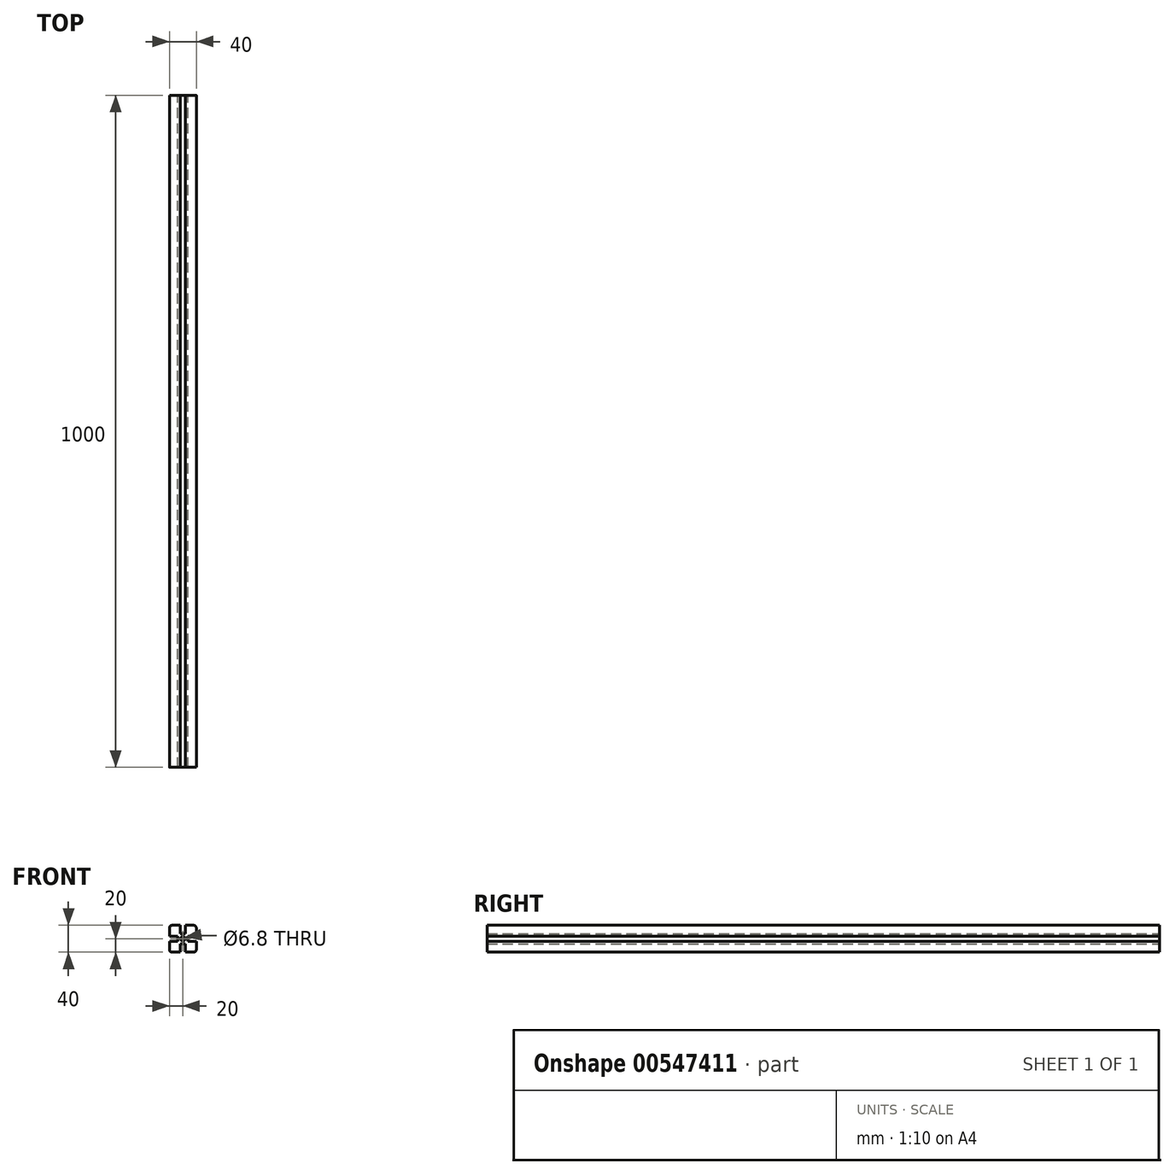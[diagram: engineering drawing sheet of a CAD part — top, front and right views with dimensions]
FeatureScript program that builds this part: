
annotation { "Feature Type Name" : "Feature", "Feature Type Description" : "" }
export const myFeature = defineFeature(function(context is Context, id is Id, definition is map)
    precondition{}
    {
        {
            var Q0;
            Q0=qCreatedBy(makeId("Front.planeOp"),FACE);
            var sketch = newSketch(context, id + "F0", { "sketchPlane" : qUnion([Q0])});
            skLineSegment(sketch, "E0.bottom", {"start": v(20, 20) * mm, "end": v(4, 20) * mm});
            skLineSegment(sketch, "E0.top", {"start": v(20, -20) * mm, "end": v(4, -20) * mm});
            skLineSegment(sketch, "E0.left", {"start": v(20, 20) * mm, "end": v(20, 4) * mm});
            skLineSegment(sketch, "E0.right", {"start": v(-20, 20) * mm, "end": v(-20, 4) * mm});
            skPoint(sketch, "E0.middle", {"position": v(0, 0) * mm});
            skLineSegment(sketch, "E1", {"start": v(20, 4) * mm, "end": v(7.75, 4) * mm});
            skLineSegment(sketch, "E2", {"start": v(7.75, 4) * mm, "end": v(7.75, -4) * mm});
            skLineSegment(sketch, "E3", {"start": v(7.75, -4) * mm, "end": v(20, -4) * mm});
            skLineSegment(sketch, "E4.top", {"start": v(-4, 7.75) * mm, "end": v(4, 7.75) * mm});
            skLineSegment(sketch, "E4.left", {"start": v(-4, 20) * mm, "end": v(-4, 7.75) * mm});
            skLineSegment(sketch, "E4.right", {"start": v(4, 20) * mm, "end": v(4, 7.75) * mm});
            skLineSegment(sketch, "E5.bottom", {"start": v(-20, 4) * mm, "end": v(-7.75, 4) * mm});
            skLineSegment(sketch, "E5.top", {"start": v(-20, -4) * mm, "end": v(-7.75, -4) * mm});
            skLineSegment(sketch, "E5.right", {"start": v(-7.75, 4) * mm, "end": v(-7.75, -4) * mm});
            skLineSegment(sketch, "E6.top", {"start": v(-4, -7.75) * mm, "end": v(4, -7.75) * mm});
            skLineSegment(sketch, "E6.left", {"start": v(-4, -20) * mm, "end": v(-4, -7.75) * mm});
            skLineSegment(sketch, "E6.right", {"start": v(4, -20) * mm, "end": v(4, -7.75) * mm});
            skLineSegment(sketch, "E7.trimOffspring", {"start": v(-4, 20) * mm, "end": v(-20, 20) * mm});
            skLineSegment(sketch, "E8.trimOffspring", {"start": v(-20, -4) * mm, "end": v(-20, -20) * mm});
            skLineSegment(sketch, "E9.trimOffspring", {"start": v(-4, -20) * mm, "end": v(-20, -20) * mm});
            skLineSegment(sketch, "E10.trimOffspring", {"start": v(20, -4) * mm, "end": v(20, -20) * mm});
            skSolve(sketch);
        }
        {
            var Q0;
            Q0 = qSketchRegion(id + "F0", true);
            extrude(context, id + "F1", {"entities" : qUnion([Q0]), "endBound" : BoundingType.SYMMETRIC, "depth" : 1000 * mm, "offsetDistance" : 25 * mm});
        }
        {
            var Q0;
            Q0=makeQuery(id+"F1.opExtrude","SWEPT_EDGE",EDGE,{"disambiguationData":[OSD([sQuery(id+"F0.wireOp",EDGE,"E0.right"),sQuery(id+"F0.wireOp",EDGE,"E7.trimOffspring")])]});
            var Q1;
            Q1=makeQuery(id+"F1.opExtrude","SWEPT_EDGE",EDGE,{"disambiguationData":[OSD([sQuery(id+"F0.wireOp",EDGE,"E0.bottom"),sQuery(id+"F0.wireOp",EDGE,"E0.left")])]});
            var Q2;
            Q2=makeQuery(id+"F1.opExtrude","SWEPT_EDGE",EDGE,{"disambiguationData":[OSD([sQuery(id+"F0.wireOp",EDGE,"E0.top"),sQuery(id+"F0.wireOp",EDGE,"E10.trimOffspring")])]});
            var Q3;
            Q3=makeQuery(id+"F1.opExtrude","SWEPT_EDGE",EDGE,{"disambiguationData":[OSD([sQuery(id+"F0.wireOp",EDGE,"E8.trimOffspring"),sQuery(id+"F0.wireOp",EDGE,"E9.trimOffspring")])]});
            fillet(context, id + "F2", {"entities" : qUnion([Q0, Q1, Q2, Q3]), "radius" : 4 * mm, "tangentPropagation" : true, "allowEdgeOverflow" : false});
        }
        {
            var Q0;
            Q0=makeQuery(id+"F1.opExtrude","CAP_FACE",FACE,{"disambiguationData":[OSD([sQuery(id+"F0.wireOp",EDGE,"E0.bottom"),sQuery(id+"F0.wireOp",EDGE,"E0.top"),sQuery(id+"F0.wireOp",EDGE,"E0.left"),sQuery(id+"F0.wireOp",EDGE,"E0.right"),sQuery(id+"F0.wireOp",EDGE,"E1"),sQuery(id+"F0.wireOp",EDGE,"E2"),sQuery(id+"F0.wireOp",EDGE,"E3"),sQuery(id+"F0.wireOp",EDGE,"E4.top"),sQuery(id+"F0.wireOp",EDGE,"E4.left"),sQuery(id+"F0.wireOp",EDGE,"E4.right"),sQuery(id+"F0.wireOp",EDGE,"E5.bottom"),sQuery(id+"F0.wireOp",EDGE,"E5.top"),sQuery(id+"F0.wireOp",EDGE,"E5.right"),sQuery(id+"F0.wireOp",EDGE,"E6.top"),sQuery(id+"F0.wireOp",EDGE,"E6.left"),sQuery(id+"F0.wireOp",EDGE,"E6.right"),sQuery(id+"F0.wireOp",EDGE,"E7.trimOffspring"),sQuery(id+"F0.wireOp",EDGE,"E8.trimOffspring"),sQuery(id+"F0.wireOp",EDGE,"E9.trimOffspring"),sQuery(id+"F0.wireOp",EDGE,"E10.trimOffspring")])],"isStart":false});
            var sketch = newSketch(context, id + "F3", { "sketchPlane" : qUnion([Q0])});
            skCircle(sketch, "E11", {"center": v(0, 0) * mm, "radius": 3.4 * mm});
            skSolve(sketch);
        }
        {
            var Q0;
            Q0 = qSketchRegion(id + "F3", true);
            extrude(context, id + "F4", {"entities" : qUnion([Q0]), "operationType" : NewBodyOperationType.REMOVE, "oppositeDirection" : true, "depth" : 1000 * mm, "offsetDistance" : 25 * mm});
        }
    });
